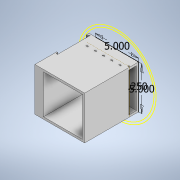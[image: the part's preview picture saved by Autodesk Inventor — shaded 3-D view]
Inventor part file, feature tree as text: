
AUTODESK INVENTOR PART (.ipt)
format: ipt  version: 2022 (Build 260153000, 153)  size: 279,552 bytes
history: native  units: in
note: dims shown in document units (in); Inventor stores cm internally (conversion verified against a paired STEP export)
features: sketch x16, extrude x15, reference x3, projected_geometry x3, other x3, plane x1
ambient origin geometry x8: Origin, YZ Plane, XZ Plane, XY Plane, X Axis, Y Axis, Z Axis, Center Point
bodies: Solid1 (feature_tree)
feature tree (41):
  extrude  "Extrusion1"  Depth=5.0in
  extrude  "Extrusion2"  Depth=0.25in TaperAngle=0.0deg
  extrude  "Extrusion3"  Depth=6.0in TaperAngle=0.0deg
  extrude  "Extrusion4"  Depth=1.5in
  plane  "Work Plane1"
  extrude  "Extrusion5"  Depth=0.25in
  extrude  "Extrusion6"  Depth=0.5in
  extrude  "Extrusion7"  Depth=0.75in
  extrude  "Extrusion8"  Depth=0.25in
  extrude  "Extrusion9"  Depth=0.3937in
  extrude  "Extrusion10"  Depth=0.25in TaperAngle=0.0deg
  sketch  "Sketch12"  dims[d34=0.125in d35=0.125in]
  extrude  "Extrusion11"  Depth=0.125in
  extrude  "Extrusion12"  Depth=4.5in TaperAngle=0.0deg
  extrude  "Extrusion13"  Depth=0.125in TaperAngle=0.0deg
  extrude  "Extrusion14"  Depth=0.875in TaperAngle=0.0deg
  extrude  "Extrusion15"  Depth=4.8125in TaperAngle=0.0deg
  sketch  "Sketch1"  dims[d0=5.0in d1=5.0in]
  reference  "Reference1"
  reference  "Reference2"
  reference  "Reference3"
  sketch  "Sketch2"  dims[d2=0.25in d3=0.25in d4=0.0in]
  sketch  "Sketch3"  dims[d5=0.25in d6=6.0in d7=0.0in]
  projected_geometry  "Projected Loop1"
  sketch  "Sketch4"  dims[d8=0.75in d9=0.0in d10=1.5in]
  sketch  "Sketch6"  dims[d11=4.5in d12=0.25in]
  projected_geometry  "Projected Loop2"
  sketch  "Sketch7"  dims[d13=0.25in d14=0.5in]
  sketch  "Sketch8"  dims[d15=0.3in d16=0.0in d17=0.75in]
  sketch  "Sketch9"  dims[d18=0.25in d19=0.0in d20=0.25in]
  projected_geometry  "Projected Loop3"
  sketch  "Sketch10"  dims[d21=0.5in d22=1.9685in d24=0.95in d25=0.3937in d27=1.0in]
  sketch  "Sketch11"  dims[d29=5.0in d30=0.0in d31=0.25in d32=0.0in]
  sketch  "Sketch13"  dims[d36=10.0in d37=0.0in d38=4.5in d39=0.0in]
  sketch  "Sketch14"  dims[d40=0.125in d41=1.6875in d42=0.0in]
  sketch  "Sketch16"  dims[d43=0.875in d44=0.0in d45=0.875in d46=0.0in]
  sketch  "Sketch17"  dims[d47=4.8125in d48=0.0in d49=4.8125in d50=0.0in]
  sketch  "Sketch19"  dims[d53=0.025in d54=0.3in d55=0.025in d56=0.3in d57=0.025in d58=1.875in d59=0.0in]
  other  "<userpath>\OneDrive\Desktop\Smarty Plants Files\Assembly1.iam"
  other  "Assembly1.iam"
  other  "Drainage Base:1"
